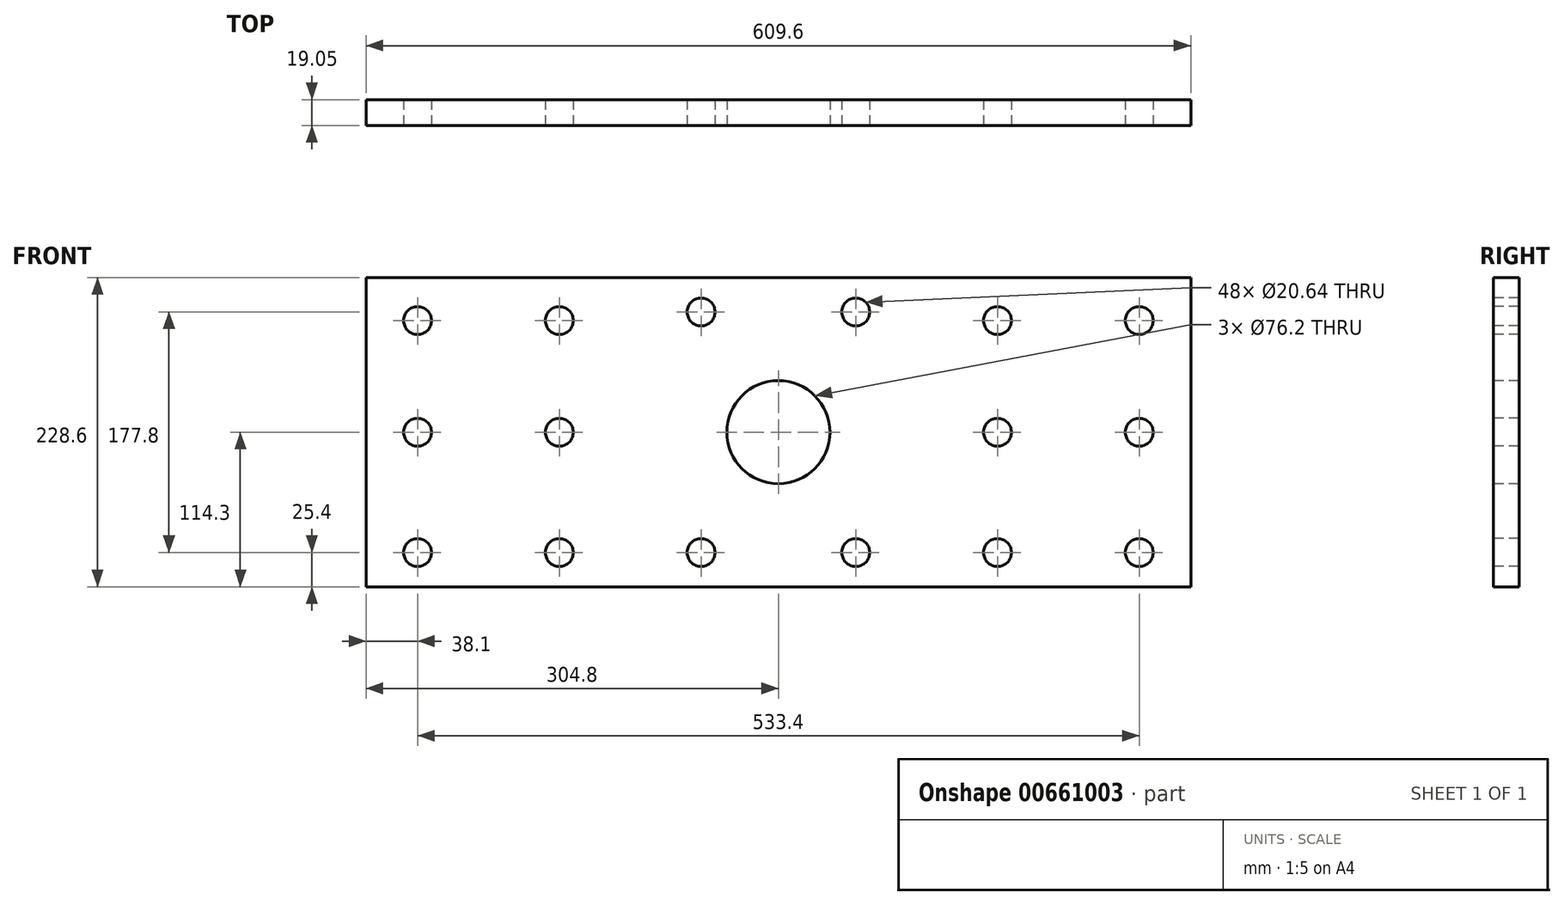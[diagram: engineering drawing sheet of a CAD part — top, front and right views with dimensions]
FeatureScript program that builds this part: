
annotation { "Feature Type Name" : "Feature", "Feature Type Description" : "" }
export const myFeature = defineFeature(function(context is Context, id is Id, definition is map)
    precondition{}
    {
        {
            var Q0;
            Q0=qCreatedBy(makeId("Front.planeOp"),FACE);
            var sketch = newSketch(context, id + "F0", { "sketchPlane" : qUnion([Q0])});
            skLineSegment(sketch, "E0", {"start": v(0, 0) * mm, "end": v(-609.6, 0) * mm, "construction": true});
            skLineSegment(sketch, "E1", {"start": v(0, 0) * mm, "end": v(0, 38.1) * mm, "construction": true});
            skCircle(sketch, "E2", {"center": v(0, 38.1) * mm, "radius": 38.1 * mm});
            skCircle(sketch, "E3", {"center": v(0, 38.1) * mm, "radius": 57.15 * mm});
            skCircle(sketch, "E4", {"center": v(161.93, 38.1) * mm, "radius": 10.32 * mm});
            skCircle(sketch, "E5", {"center": v(266.7, 38.1) * mm, "radius": 10.32 * mm});
            skCircle(sketch, "E6", {"center": v(161.93, -50.8) * mm, "radius": 10.32 * mm});
            skCircle(sketch, "E7", {"center": v(266.7, -50.8) * mm, "radius": 10.32 * mm});
            skCircle(sketch, "E8", {"center": v(57.15, 127) * mm, "radius": 10.32 * mm});
            skCircle(sketch, "E9", {"center": v(161.93, 120.65) * mm, "radius": 10.32 * mm});
            skCircle(sketch, "E10", {"center": v(266.7, 120.65) * mm, "radius": 10.32 * mm});
            skCircle(sketch, "E11", {"center": v(57.15, -50.8) * mm, "radius": 10.32 * mm});
            skLineSegment(sketch, "E12", {"start": v(0, 0) * mm, "end": v(0, 368.3) * mm, "construction": true});
            skCircle(sketch, "E13.MirrorC", {"center": v(-57.15, 127) * mm, "radius": 10.32 * mm});
            skCircle(sketch, "E14.MirrorC", {"center": v(-161.93, 120.65) * mm, "radius": 10.32 * mm});
            skCircle(sketch, "E15.MirrorC", {"center": v(-266.7, 120.65) * mm, "radius": 10.32 * mm});
            skCircle(sketch, "E16.MirrorC", {"center": v(-266.7, 38.1) * mm, "radius": 10.32 * mm});
            skCircle(sketch, "E17.MirrorC", {"center": v(-161.93, 38.1) * mm, "radius": 10.32 * mm});
            skCircle(sketch, "E18.MirrorC", {"center": v(-266.7, -50.8) * mm, "radius": 10.32 * mm});
            skCircle(sketch, "E19.MirrorC", {"center": v(-161.93, -50.8) * mm, "radius": 10.32 * mm});
            skCircle(sketch, "E20.MirrorC", {"center": v(-57.15, -50.8) * mm, "radius": 10.32 * mm});
            skLineSegment(sketch, "E21.bottom", {"start": v(304.8, 152.4) * mm, "end": v(-304.8, 152.4) * mm});
            skLineSegment(sketch, "E21.top", {"start": v(304.8, -76.2) * mm, "end": v(-304.8, -76.2) * mm});
            skLineSegment(sketch, "E21.left", {"start": v(304.8, 152.4) * mm, "end": v(304.8, -76.2) * mm});
            skLineSegment(sketch, "E21.right", {"start": v(-304.8, 152.4) * mm, "end": v(-304.8, -76.2) * mm});
            skLineSegment(sketch, "E22", {"start": v(0, 0) * mm, "end": v(609.6, 0) * mm, "construction": true});
            skSolve(sketch);
        }
        {
            var Q0;
            Q0=makeQuery(id+"F0.imprint","IMPRINT",FACE,{"disambiguationData":[TD([[makeQuery(id+"F0.imprint","IMPRINT",EDGE,{"derivedFrom":sQuery(id+"F0.wireOp",EDGE,"E3")}),-1.0]])]});
            var Q1;
            Q1=makeQuery(id+"F0.imprint","IMPRINT",FACE,{"disambiguationData":[TD([[makeQuery(id+"F0.imprint","IMPRINT",EDGE,{"derivedFrom":sQuery(id+"F0.wireOp",EDGE,"E2")}),-1.0]])]});
            extrude(context, id + "F1", {"entities" : qUnion([Q0, Q1]), "oppositeDirection" : true, "depth" : 19.05 * mm, "offsetDistance" : 25.4 * mm});
        }
    });
